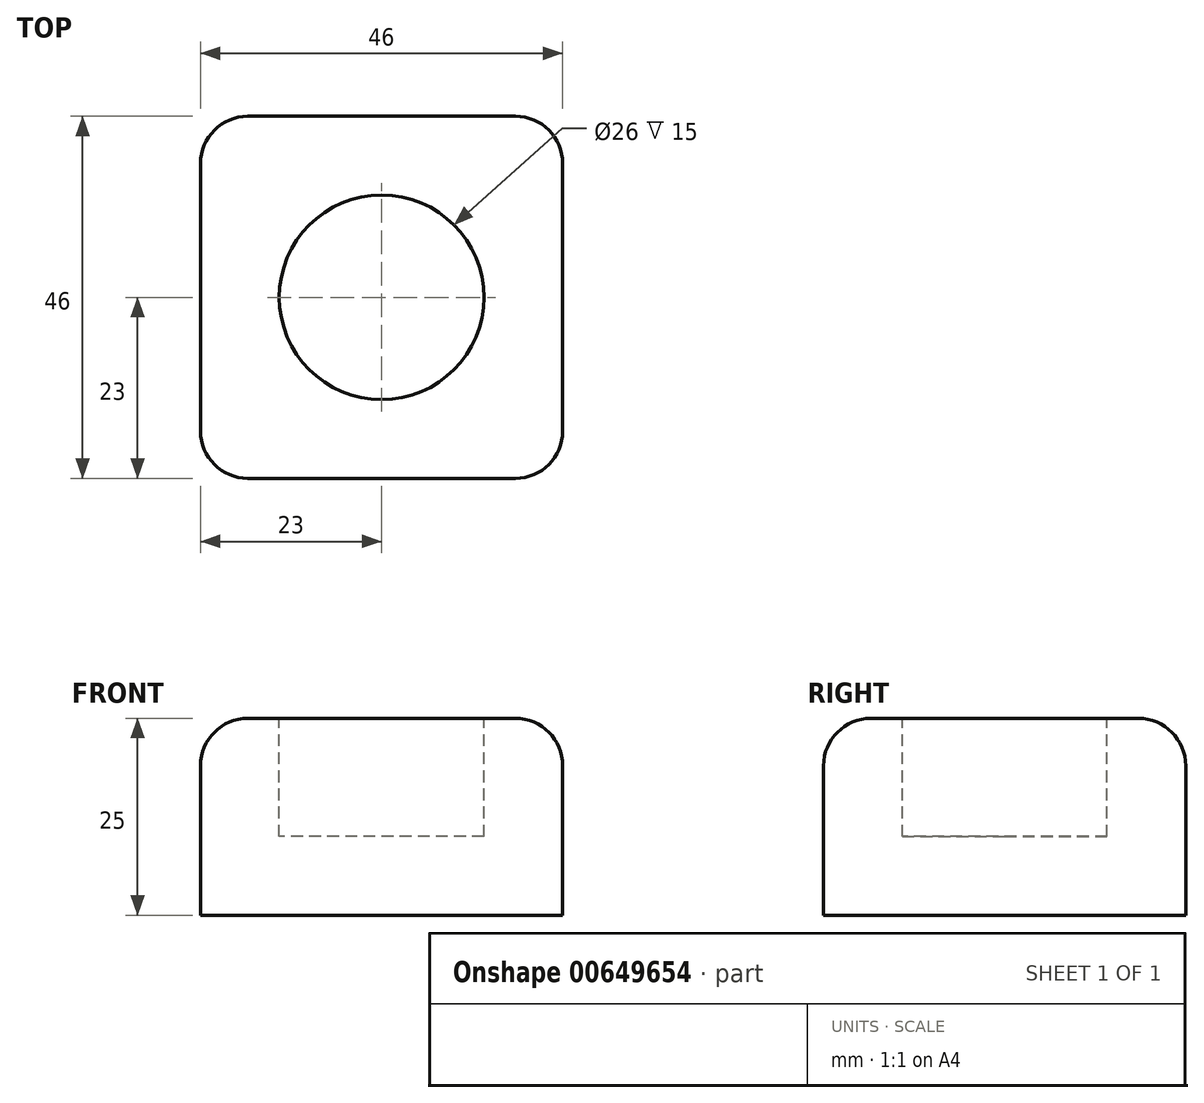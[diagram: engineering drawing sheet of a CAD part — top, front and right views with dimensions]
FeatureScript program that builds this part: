
annotation { "Feature Type Name" : "Feature", "Feature Type Description" : "" }
export const myFeature = defineFeature(function(context is Context, id is Id, definition is map)
    precondition{}
    {
        {
            var Q0;
            Q0=qCreatedBy(makeId("Top.planeOp"),FACE);
            var sketch = newSketch(context, id + "F0", { "sketchPlane" : qUnion([Q0])});
            skLineSegment(sketch, "E0.bottom", {"start": v(0, 0) * mm, "end": v(-46, 0) * mm});
            skLineSegment(sketch, "E0.top", {"start": v(0, 46) * mm, "end": v(-46, 46) * mm});
            skLineSegment(sketch, "E0.left", {"start": v(0, 0) * mm, "end": v(0, 46) * mm});
            skLineSegment(sketch, "E0.right", {"start": v(-46, 0) * mm, "end": v(-46, 46) * mm});
            skSolve(sketch);
        }
        {
            var Q0;
            Q0=qSketchRegion(id+"F0",true);
            extrude(context, id + "F1", {"entities" : qUnion([Q0]), "depth" : 25 * mm, "offsetDistance" : 25 * mm});
        }
        {
            var Q0;
            Q0=makeQuery(id+"F1.opExtrude","CAP_FACE",FACE,{"disambiguationData":[OSD([sQuery(id+"F0.wireOp",EDGE,"E0.bottom"),sQuery(id+"F0.wireOp",EDGE,"E0.top"),sQuery(id+"F0.wireOp",EDGE,"E0.left"),sQuery(id+"F0.wireOp",EDGE,"E0.right")])],"isStart":false});
            var sketch = newSketch(context, id + "F2", { "sketchPlane" : qUnion([Q0])});
            skLineSegment(sketch, "E1", {"start": v(-46, 0) * mm, "end": v(-23, 0) * mm});
            skLineSegment(sketch, "E2", {"start": v(-23, 0) * mm, "end": v(-23, 23) * mm});
            skPoint(sketch, "E2.endSnap0", {"position": v(-23, 46) * mm});
            skCircle(sketch, "E3", {"center": v(-23, 23) * mm, "radius": 13 * mm});
            skSolve(sketch);
        }
        {
            var Q0;
            Q0=makeQuery(id+"F2.imprint","IMPRINT",FACE,{"disambiguationData":[TD([[makeQuery(id+"F2.imprint","IMPRINT",EDGE,{"derivedFrom":sQuery(id+"F2.wireOp",EDGE,"E3")}),1.0]])]});
            extrude(context, id + "F3", {"entities" : qUnion([Q0]), "operationType" : NewBodyOperationType.REMOVE, "oppositeDirection" : true, "depth" : 15 * mm, "offsetDistance" : 25 * mm});
        }
        {
            var Q0;
            Q0=makeQuery(id+"F1.opExtrude","CAP_EDGE",EDGE,{"disambiguationData":[OSD([sQuery(id+"F0.wireOp",EDGE,"E0.bottom")])],"isStart":false});
            var Q1;
            Q1=makeQuery(id+"F1.opExtrude","CAP_EDGE",EDGE,{"disambiguationData":[OSD([sQuery(id+"F0.wireOp",EDGE,"E0.right")])],"isStart":false});
            var Q2;
            Q2=makeQuery(id+"F1.opExtrude","CAP_EDGE",EDGE,{"disambiguationData":[OSD([sQuery(id+"F0.wireOp",EDGE,"E0.left")])],"isStart":false});
            var Q3;
            Q3=makeQuery(id+"F1.opExtrude","CAP_EDGE",EDGE,{"disambiguationData":[OSD([sQuery(id+"F0.wireOp",EDGE,"E0.top")])],"isStart":false});
            fillet(context, id + "F4", {"entities" : qUnion([Q0, Q1, Q2, Q3]), "radius" : 6 * mm, "tangentPropagation" : true, "allowEdgeOverflow" : false});
        }
        {
            var Q0;
            Q0=makeQuery(id+"F1.opExtrude","SWEPT_EDGE",EDGE,{"disambiguationData":[OSD([sQuery(id+"F0.wireOp",EDGE,"E0.bottom"),sQuery(id+"F0.wireOp",EDGE,"E0.right")])]});
            var Q1;
            Q1=makeQuery(id+"F1.opExtrude","SWEPT_EDGE",EDGE,{"disambiguationData":[OSD([sQuery(id+"F0.wireOp",EDGE,"E0.bottom"),sQuery(id+"F0.wireOp",EDGE,"E0.left")])]});
            var Q2;
            Q2=makeQuery(id+"F1.opExtrude","SWEPT_EDGE",EDGE,{"disambiguationData":[OSD([sQuery(id+"F0.wireOp",EDGE,"E0.top"),sQuery(id+"F0.wireOp",EDGE,"E0.left")])]});
            var Q3;
            Q3=makeQuery(id+"F1.opExtrude","SWEPT_EDGE",EDGE,{"disambiguationData":[OSD([sQuery(id+"F0.wireOp",EDGE,"E0.top"),sQuery(id+"F0.wireOp",EDGE,"E0.right")])]});
            fillet(context, id + "F5", {"entities" : qUnion([Q0, Q1, Q2, Q3]), "radius" : 6 * mm, "tangentPropagation" : true, "allowEdgeOverflow" : false});
        }
    });
